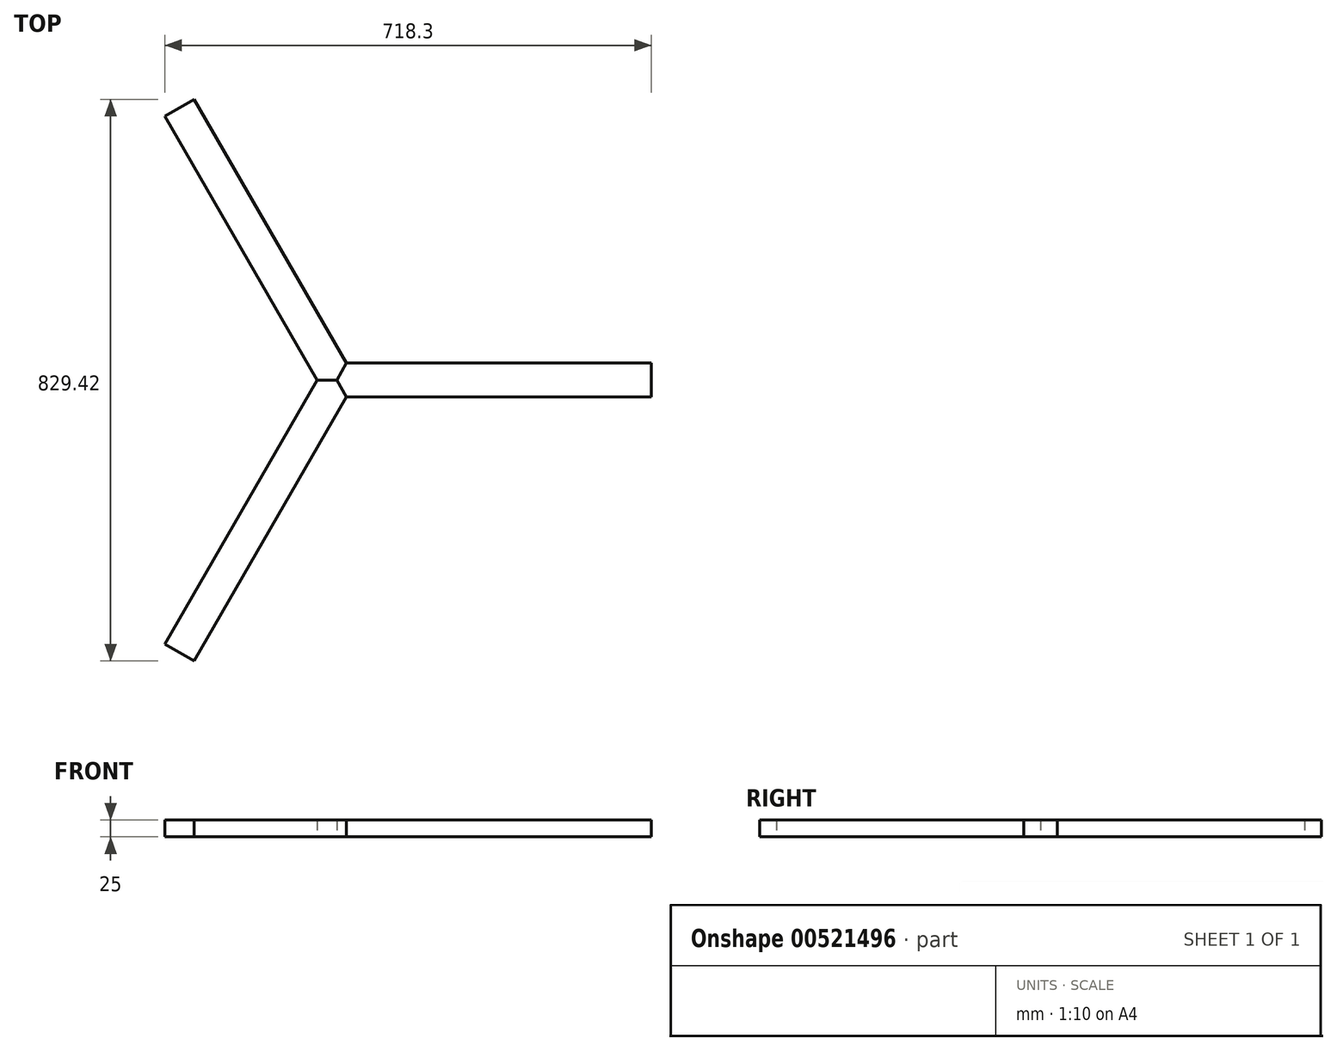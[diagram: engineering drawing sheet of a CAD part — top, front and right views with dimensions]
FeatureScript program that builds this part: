
annotation { "Feature Type Name" : "Feature", "Feature Type Description" : "" }
export const myFeature = defineFeature(function(context is Context, id is Id, definition is map)
    precondition{}
    {
        {
            var Q0;
            Q0=qCreatedBy(makeId("Top.planeOp"),FACE);
            var sketch = newSketch(context, id + "F0", { "sketchPlane" : qUnion([Q0])});
            skLineSegment(sketch, "E0", {"start": v(0, 0) * mm, "end": v(14.43, 25) * mm});
            skLineSegment(sketch, "E1", {"start": v(14.43, 25) * mm, "end": v(464.43, 25) * mm});
            skLineSegment(sketch, "E2", {"start": v(464.43, 25) * mm, "end": v(464.43, -25) * mm});
            skLineSegment(sketch, "E3", {"start": v(464.43, -25) * mm, "end": v(14.43, -25) * mm});
            skLineSegment(sketch, "E4", {"start": v(14.43, -25) * mm, "end": v(0, 0) * mm});
            skSolve(sketch);
        }
        {
            var Q0;
            Q0=qCreatedBy(makeId("Front.planeOp"),FACE);
            var sketch = newSketch(context, id + "F1", { "sketchPlane" : qUnion([Q0])});
            skLineSegment(sketch, "E5", {"start": v(0, 0) * mm, "end": v(0, 139.5) * mm, "construction": true});
            skSolve(sketch);
        }
        {
            var Q0;
            Q0 = qSketchRegion(id + "F0", true);
            extrude(context, id + "F2", {"entities" : qUnion([Q0]), "depth" : 25 * mm, "offsetDistance" : 25 * mm});
        }
        {
            var Q0;
            Q0=makeQuery(id+"F2.opExtrude","SWEPT_BODY",BODY,{"disambiguationData":[OSD([sQuery(id+"F0.wireOp",EDGE,"E0"),sQuery(id+"F0.wireOp",EDGE,"E1"),sQuery(id+"F0.wireOp",EDGE,"E2"),sQuery(id+"F0.wireOp",EDGE,"E3"),sQuery(id+"F0.wireOp",EDGE,"E4")])]});
            var Q1;
            Q1=sQuery(id+"F1.wireOp",EDGE,"E5");
            circularPattern(context, id + "F3", {"entities" : qUnion([Q0]), "axis" : qUnion([Q1]), "angle" : 360 * degree, "instanceCount" : 3, "equalSpace" : true});
        }
    });
